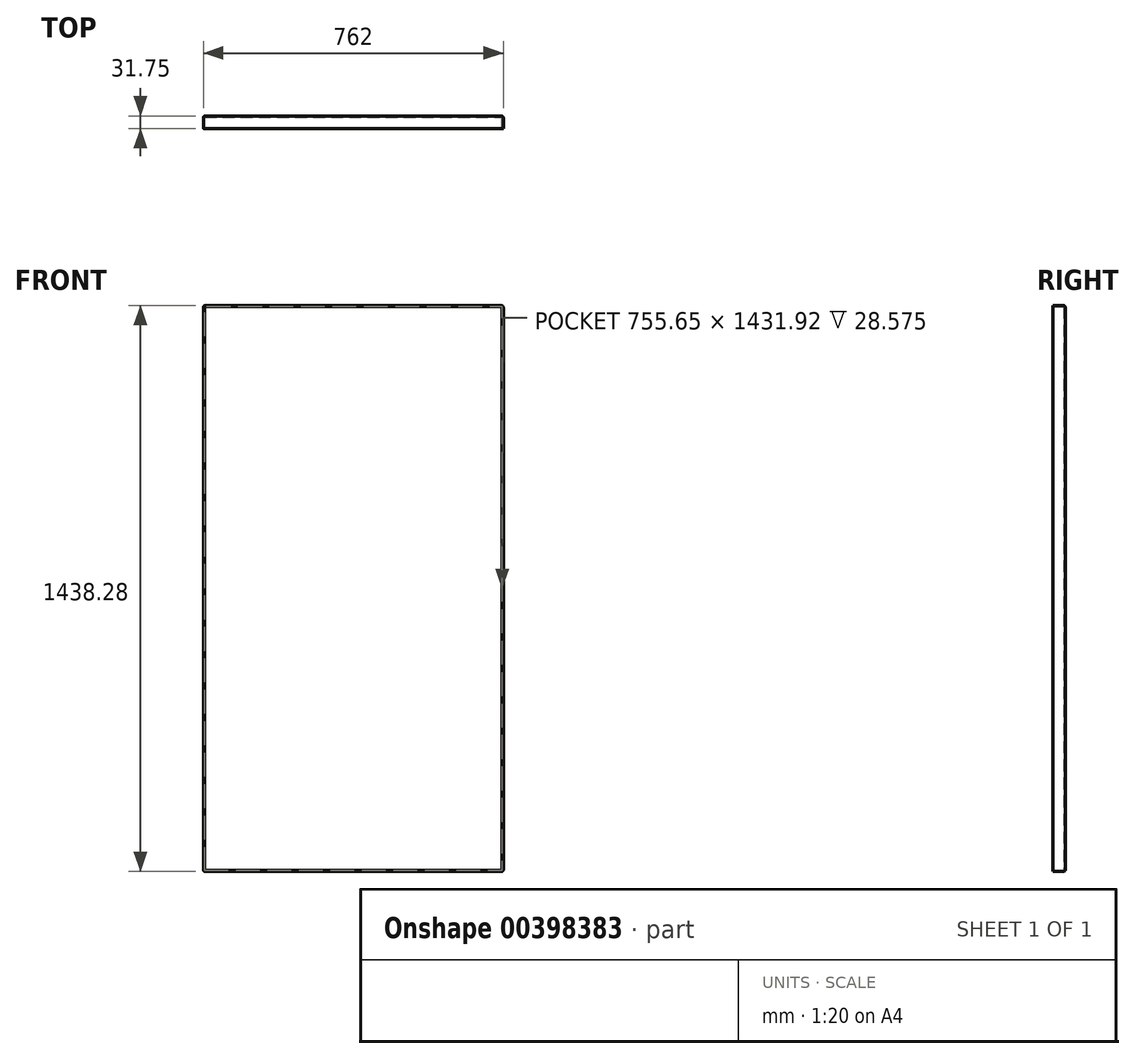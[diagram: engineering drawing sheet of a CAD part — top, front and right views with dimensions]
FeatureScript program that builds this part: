
annotation { "Feature Type Name" : "Feature", "Feature Type Description" : "" }
export const myFeature = defineFeature(function(context is Context, id is Id, definition is map)
    precondition{}
    {
        {
            var Q0;
            Q0=qCreatedBy(makeId("Front.planeOp"),FACE);
            var sketch = newSketch(context, id + "F0", { "sketchPlane" : qUnion([Q0])});
            skLineSegment(sketch, "E0.bottom", {"start": v(-381, -719.14) * mm, "end": v(381, -719.14) * mm});
            skLineSegment(sketch, "E0.top", {"start": v(-381, 719.14) * mm, "end": v(381, 719.14) * mm});
            skLineSegment(sketch, "E0.left", {"start": v(-381, -719.14) * mm, "end": v(-381, 719.14) * mm});
            skLineSegment(sketch, "E0.right", {"start": v(381, -719.14) * mm, "end": v(381, 719.14) * mm});
            skPoint(sketch, "E0.middle", {"position": v(0, 0) * mm});
            skSolve(sketch);
        }
        {
            var Q0;
            Q0 = qSketchRegion(id + "F0", true);
            extrude(context, id + "F1", {"entities" : qUnion([Q0]), "depth" : 3.17 * mm});
        }
        {
            var Q0;
            Q0=makeQuery(id+"F1.opExtrude","CAP_FACE",FACE,{"disambiguationData":[OSD([sQuery(id+"F0.wireOp",EDGE,"E0.bottom"),sQuery(id+"F0.wireOp",EDGE,"E0.top"),sQuery(id+"F0.wireOp",EDGE,"E0.left"),sQuery(id+"F0.wireOp",EDGE,"E0.right")])],"isStart":false});
            var sketch = newSketch(context, id + "F2", { "sketchPlane" : qUnion([Q0])});
            skLineSegment(sketch, "E1.bottom", {"start": v(-381, 719.14) * mm, "end": v(381, 719.14) * mm});
            skLineSegment(sketch, "E1.top", {"start": v(-381, -719.14) * mm, "end": v(381, -719.14) * mm});
            skLineSegment(sketch, "E1.left", {"start": v(-381, 719.14) * mm, "end": v(-381, -719.14) * mm});
            skLineSegment(sketch, "E1.right", {"start": v(381, 719.14) * mm, "end": v(381, -719.14) * mm});
            skLineSegment(sketch, "E2.bottom", {"start": v(-377.83, 715.96) * mm, "end": v(377.83, 715.96) * mm});
            skLineSegment(sketch, "E2.top", {"start": v(-377.83, -715.96) * mm, "end": v(377.83, -715.96) * mm});
            skLineSegment(sketch, "E2.left", {"start": v(-377.83, 715.96) * mm, "end": v(-377.83, -715.96) * mm});
            skLineSegment(sketch, "E2.right", {"start": v(377.83, 715.96) * mm, "end": v(377.83, -715.96) * mm});
            skSolve(sketch);
        }
        {
            var Q0;
            Q0 = qSketchRegion(id + "F2", true);
            extrude(context, id + "F3", {"entities" : qUnion([Q0]), "operationType" : NewBodyOperationType.ADD, "depth" : 28.57 * mm});
        }
        {
            var Q0;
            Q0=makeQuery(id+"F1.opExtrude","CAP_EDGE",EDGE,{"disambiguationData":[OSD([sQuery(id+"F0.wireOp",EDGE,"E0.bottom")])],"isStart":true});
            var Q1;
            Q1=makeQuery(id+"F1.opExtrude","CAP_EDGE",EDGE,{"disambiguationData":[OSD([sQuery(id+"F0.wireOp",EDGE,"E0.right")])],"isStart":true});
            var Q2;
            Q2=makeQuery(id+"F1.opExtrude","CAP_EDGE",EDGE,{"disambiguationData":[OSD([sQuery(id+"F0.wireOp",EDGE,"E0.left")])],"isStart":true});
            var Q3;
            Q3=makeQuery(id+"F1.opExtrude","CAP_EDGE",EDGE,{"disambiguationData":[OSD([sQuery(id+"F0.wireOp",EDGE,"E0.top")])],"isStart":true});
            fillet(context, id + "F4", {"entities" : qUnion([Q0, Q1, Q2, Q3]), "radius" : 5.08 * mm, "tangentPropagation" : true, "allowEdgeOverflow" : false});
        }
        {
            var Q0;
            Q0=makeQuery(id+"F3.boolean.opBoolean","MERGE",EDGE,{"derivedFrom":[makeQuery(id+"F1.opExtrude","SWEPT_EDGE",EDGE,{"disambiguationData":[OSD([sQuery(id+"F0.wireOp",EDGE,"E0.top"),sQuery(id+"F0.wireOp",EDGE,"E0.left")])]}),makeQuery(id+"F3.opExtrude","SWEPT_EDGE",EDGE,{"disambiguationData":[OSD([sQuery(id+"F2.wireOp",EDGE,"E1.bottom"),sQuery(id+"F2.wireOp",EDGE,"E1.left")])]})]});
            var Q1;
            Q1=makeQuery(id+"F3.boolean.opBoolean","MERGE",EDGE,{"derivedFrom":[makeQuery(id+"F1.opExtrude","SWEPT_EDGE",EDGE,{"disambiguationData":[OSD([sQuery(id+"F0.wireOp",EDGE,"E0.top"),sQuery(id+"F0.wireOp",EDGE,"E0.right")])]}),makeQuery(id+"F3.opExtrude","SWEPT_EDGE",EDGE,{"disambiguationData":[OSD([sQuery(id+"F2.wireOp",EDGE,"E1.bottom"),sQuery(id+"F2.wireOp",EDGE,"E1.right")])]})]});
            var Q2;
            Q2=makeQuery(id+"F3.boolean.opBoolean","MERGE",EDGE,{"derivedFrom":[makeQuery(id+"F1.opExtrude","SWEPT_EDGE",EDGE,{"disambiguationData":[OSD([sQuery(id+"F0.wireOp",EDGE,"E0.bottom"),sQuery(id+"F0.wireOp",EDGE,"E0.right")])]}),makeQuery(id+"F3.opExtrude","SWEPT_EDGE",EDGE,{"disambiguationData":[OSD([sQuery(id+"F2.wireOp",EDGE,"E1.top"),sQuery(id+"F2.wireOp",EDGE,"E1.right")])]})]});
            var Q3;
            Q3=makeQuery(id+"F3.boolean.opBoolean","MERGE",EDGE,{"derivedFrom":[makeQuery(id+"F1.opExtrude","SWEPT_EDGE",EDGE,{"disambiguationData":[OSD([sQuery(id+"F0.wireOp",EDGE,"E0.bottom"),sQuery(id+"F0.wireOp",EDGE,"E0.left")])]}),makeQuery(id+"F3.opExtrude","SWEPT_EDGE",EDGE,{"disambiguationData":[OSD([sQuery(id+"F2.wireOp",EDGE,"E1.top"),sQuery(id+"F2.wireOp",EDGE,"E1.left")])]})]});
            fillet(context, id + "F5", {"entities" : qUnion([Q0, Q1, Q2, Q3]), "radius" : 5.08 * mm, "tangentPropagation" : true, "allowEdgeOverflow" : false});
        }
    });
